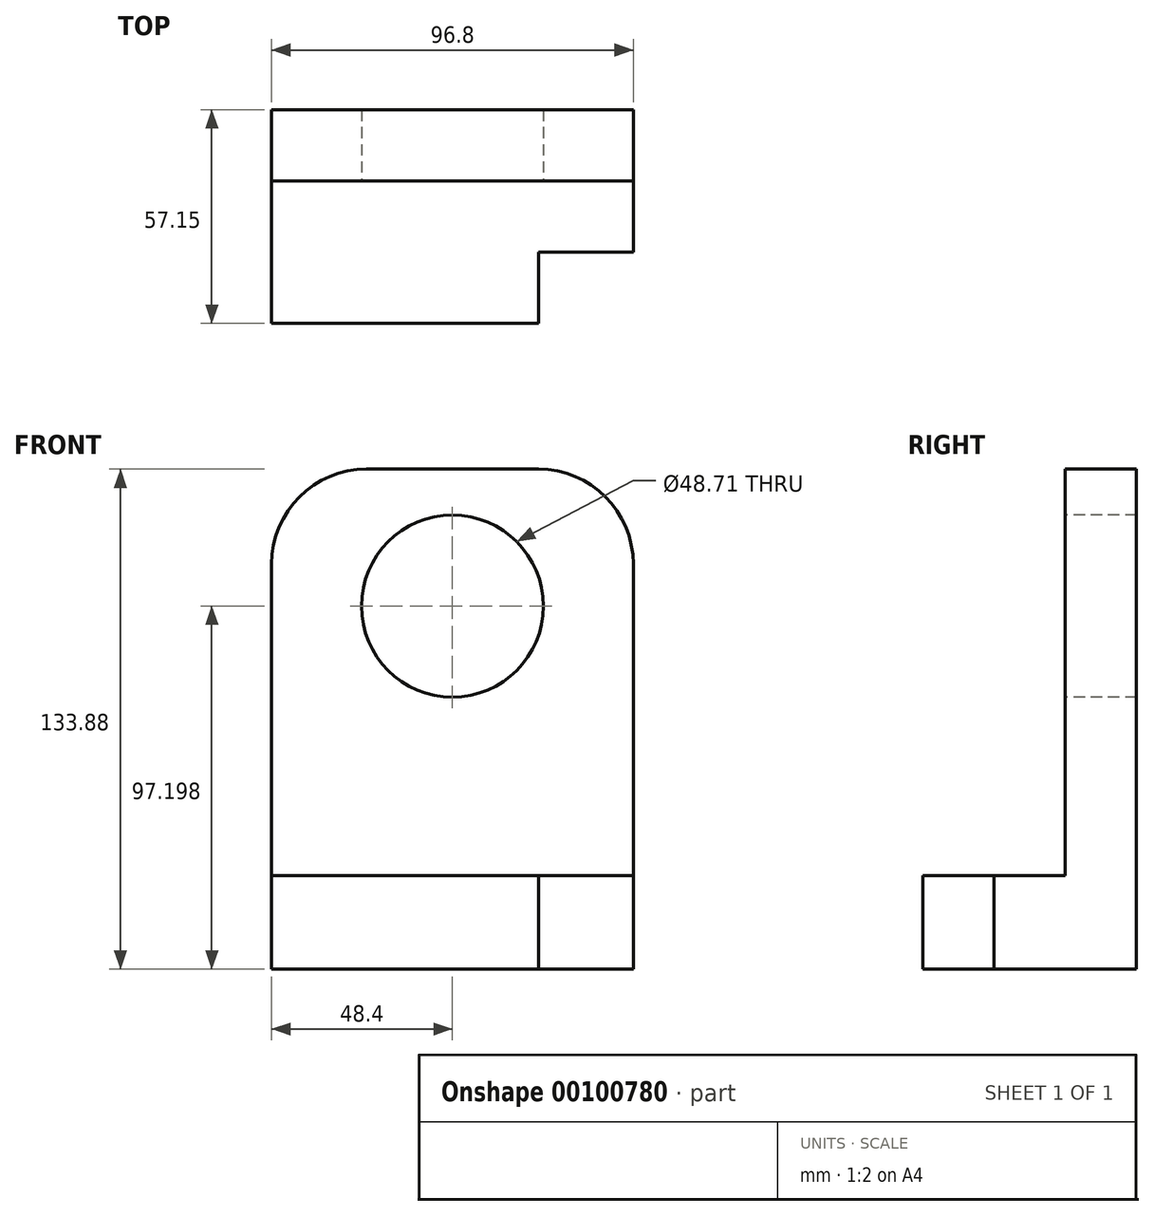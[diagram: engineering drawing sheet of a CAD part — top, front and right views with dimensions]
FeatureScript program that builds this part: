
annotation { "Feature Type Name" : "Feature", "Feature Type Description" : "" }
export const myFeature = defineFeature(function(context is Context, id is Id, definition is map)
    precondition{}
    {
        {
            var Q0;
            Q0=qCreatedBy(makeId("Front.planeOp"),FACE);
            var sketch = newSketch(context, id + "F0", { "sketchPlane" : qUnion([Q0])});
            skLineSegment(sketch, "E0.bottom", {"start": v(48.4, -66.94) * mm, "end": v(-48.4, -66.94) * mm});
            skLineSegment(sketch, "E0.top", {"start": v(48.4, 66.94) * mm, "end": v(-48.4, 66.94) * mm});
            skLineSegment(sketch, "E0.left", {"start": v(48.4, -66.94) * mm, "end": v(48.4, 66.94) * mm});
            skLineSegment(sketch, "E0.right", {"start": v(-48.4, -66.94) * mm, "end": v(-48.4, 66.94) * mm});
            skPoint(sketch, "E0.middle", {"position": v(0, 0) * mm});
            skSolve(sketch);
        }
        {
            var Q0;
            Q0=makeQuery(id+"F0.imprint","IMPRINT",FACE,{"disambiguationData":[TD([[makeQuery(id+"F0.imprint","IMPRINT",EDGE,{"derivedFrom":sQuery(id+"F0.wireOp",EDGE,"E0.bottom")}),-1.0]])]});
            extrude(context, id + "F1", {"entities" : qUnion([Q0]), "depth" : 19.05 * mm});
        }
        {
            var Q0;
            Q0=makeQuery(id+"F1.opExtrude","CAP_FACE",FACE,{"disambiguationData":[OSD([sQuery(id+"F0.wireOp",EDGE,"E0.bottom"),sQuery(id+"F0.wireOp",EDGE,"E0.top"),sQuery(id+"F0.wireOp",EDGE,"E0.left"),sQuery(id+"F0.wireOp",EDGE,"E0.right")])],"isStart":false});
            var sketch = newSketch(context, id + "F2", { "sketchPlane" : qUnion([Q0])});
            skLineSegment(sketch, "E1.bottom", {"start": v(-48.4, -41.88) * mm, "end": v(48.4, -41.88) * mm});
            skLineSegment(sketch, "E1.top", {"start": v(-48.4, -66.94) * mm, "end": v(48.4, -66.94) * mm});
            skLineSegment(sketch, "E1.left", {"start": v(-48.4, -41.88) * mm, "end": v(-48.4, -66.94) * mm});
            skLineSegment(sketch, "E1.right", {"start": v(48.4, -41.88) * mm, "end": v(48.4, -66.94) * mm});
            skSolve(sketch);
        }
        {
            var Q0;
            Q0=makeQuery(id+"F2.imprint","IMPRINT",FACE,{"disambiguationData":[TD([[makeQuery(id+"F2.imprint","IMPRINT",EDGE,{"derivedFrom":sQuery(id+"F2.wireOp",EDGE,"E1.bottom")}),-1.0]])]});
            extrude(context, id + "F3", {"entities" : qUnion([Q0]), "operationType" : NewBodyOperationType.ADD, "depth" : 38.1 * mm});
        }
        {
            var Q0;
            Q0=makeQuery(id+"F3.opExtrude","CAP_FACE",FACE,{"disambiguationData":[OSD([sQuery(id+"F2.wireOp",EDGE,"E1.bottom"),sQuery(id+"F2.wireOp",EDGE,"E1.top"),sQuery(id+"F2.wireOp",EDGE,"E1.left"),sQuery(id+"F2.wireOp",EDGE,"E1.right")])],"isStart":false});
            var sketch = newSketch(context, id + "F4", { "sketchPlane" : qUnion([Q0])});
            skLineSegment(sketch, "E2.bottom", {"start": v(23, -41.88) * mm, "end": v(48.4, -41.88) * mm});
            skLineSegment(sketch, "E2.top", {"start": v(23, -66.94) * mm, "end": v(48.4, -66.94) * mm});
            skLineSegment(sketch, "E2.left", {"start": v(23, -41.88) * mm, "end": v(23, -66.94) * mm});
            skLineSegment(sketch, "E2.right", {"start": v(48.4, -41.88) * mm, "end": v(48.4, -66.94) * mm});
            skSolve(sketch);
        }
        {
            var Q0;
            Q0=makeQuery(id+"F4.imprint","IMPRINT",FACE,{"disambiguationData":[TD([[makeQuery(id+"F4.imprint","IMPRINT",EDGE,{"derivedFrom":sQuery(id+"F4.wireOp",EDGE,"E2.bottom")}),-1.0]])]});
            extrude(context, id + "F5", {"entities" : qUnion([Q0]), "operationType" : NewBodyOperationType.REMOVE, "oppositeDirection" : true, "depth" : 19.05 * mm});
        }
        {
            var Q0;
            Q0=makeQuery(id+"F1.opExtrude","CAP_FACE",FACE,{"disambiguationData":[OSD([sQuery(id+"F0.wireOp",EDGE,"E0.bottom"),sQuery(id+"F0.wireOp",EDGE,"E0.top"),sQuery(id+"F0.wireOp",EDGE,"E0.left"),sQuery(id+"F0.wireOp",EDGE,"E0.right")])],"isStart":false});
            var sketch = newSketch(context, id + "F6", { "sketchPlane" : qUnion([Q0])});
            skCircle(sketch, "E3", {"center": v(0, 30.26) * mm, "radius": 24.36 * mm});
            skSolve(sketch);
        }
        {
            var Q0;
            Q0=makeQuery(id+"F6.imprint","IMPRINT",FACE,{"disambiguationData":[TD([[makeQuery(id+"F6.imprint","IMPRINT",EDGE,{"derivedFrom":sQuery(id+"F6.wireOp",EDGE,"E3")}),1.0]])]});
            extrude(context, id + "F7", {"entities" : qUnion([Q0]), "operationType" : NewBodyOperationType.REMOVE, "endBound" : BoundingType.THROUGH_ALL, "oppositeDirection" : true, "depth" : 25.4 * mm});
        }
        {
            var Q0;
            Q0=makeQuery(id+"F1.opExtrude","SWEPT_EDGE",EDGE,{"disambiguationData":[OSD([sQuery(id+"F0.wireOp",EDGE,"E0.top"),sQuery(id+"F0.wireOp",EDGE,"E0.right")])]});
            fillet(context, id + "F8", {"entities" : qUnion([Q0]), "radius" : 25.4 * mm, "tangentPropagation" : true, "allowEdgeOverflow" : false});
        }
        {
            var Q0;
            Q0=makeQuery(id+"F1.opExtrude","SWEPT_EDGE",EDGE,{"disambiguationData":[OSD([sQuery(id+"F0.wireOp",EDGE,"E0.top"),sQuery(id+"F0.wireOp",EDGE,"E0.left")])]});
            fillet(context, id + "F9", {"entities" : qUnion([Q0]), "radius" : 25.4 * mm, "tangentPropagation" : true, "allowEdgeOverflow" : false});
        }
    });
